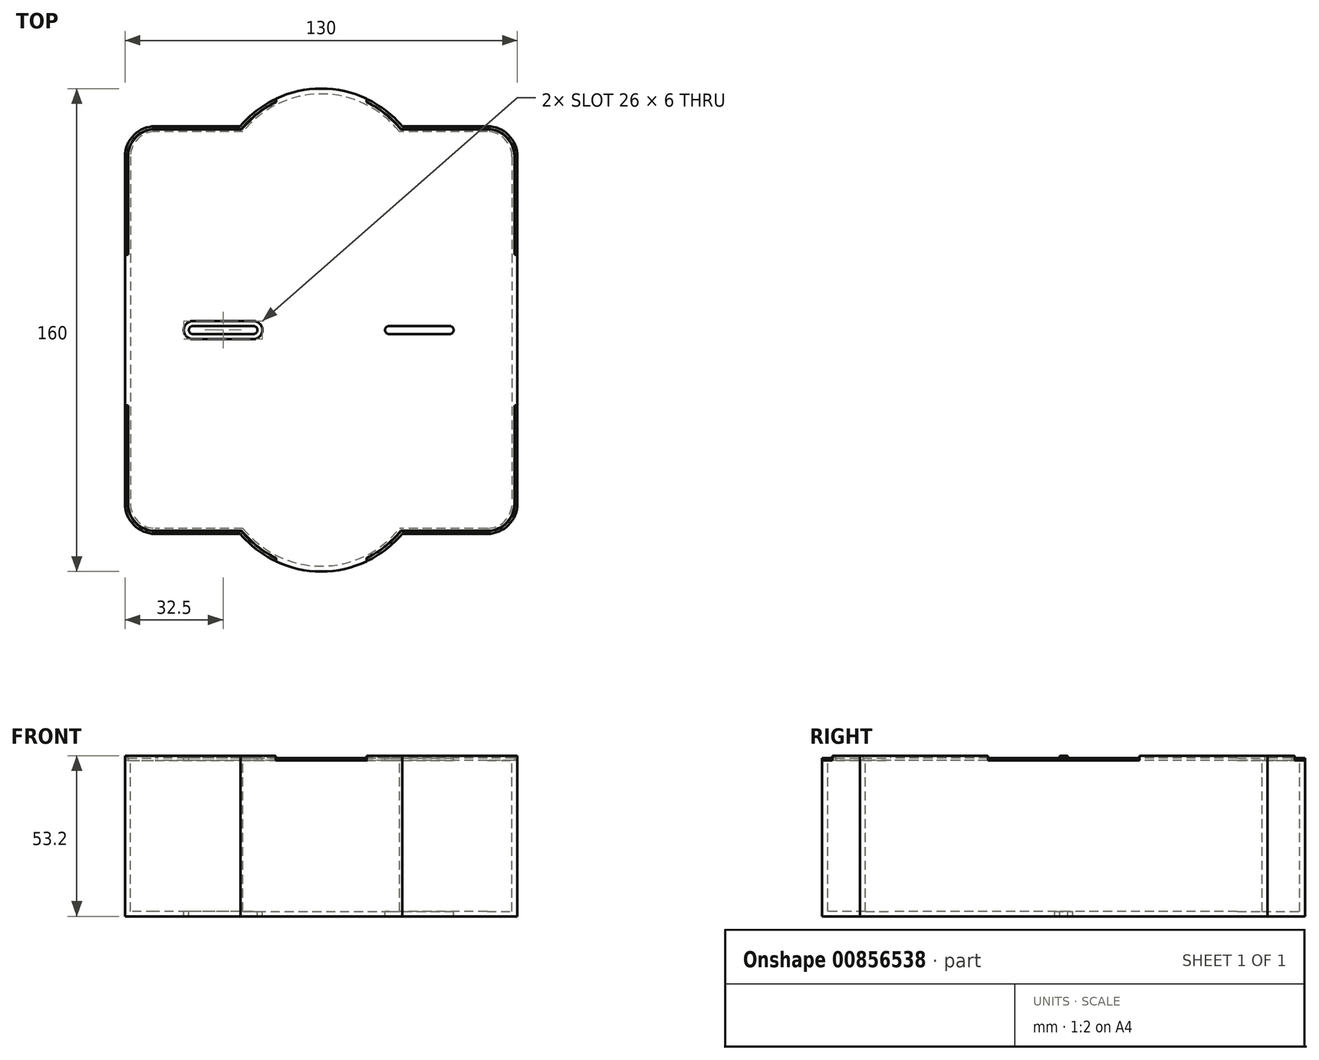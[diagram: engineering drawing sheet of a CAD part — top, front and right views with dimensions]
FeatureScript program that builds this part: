
annotation { "Feature Type Name" : "Feature", "Feature Type Description" : "" }
export const myFeature = defineFeature(function(context is Context, id is Id, definition is map)
    precondition{}
    {
        {
            var Q0;
            Q0=qCreatedBy(makeId("Top.planeOp"),FACE);
            var sketch = newSketch(context, id + "F0", { "sketchPlane" : qUnion([Q0])});
            skLineSegment(sketch, "E0.bottom", {"start": v(65, 67.5) * mm, "end": v(-65, 67.5) * mm, "construction": true});
            skLineSegment(sketch, "E0.top", {"start": v(65, -67.5) * mm, "end": v(-65, -67.5) * mm, "construction": true});
            skLineSegment(sketch, "E0.left", {"start": v(65, 67.5) * mm, "end": v(65, -67.5) * mm, "construction": true});
            skLineSegment(sketch, "E0.right", {"start": v(-65, 67.5) * mm, "end": v(-65, -67.5) * mm, "construction": true});
            skPoint(sketch, "E0.middle", {"position": v(0, 0) * mm});
            skArc(sketch, "E1", {"start": v(-26.8, 67.5) * mm, "mid": v(0, 80) * mm, "end": v(26.8, 67.5) * mm, "construction": true});
            skArc(sketch, "E2", {"start": v(-26.8, -67.5) * mm, "mid": v(0, -80) * mm, "end": v(26.8, -67.5) * mm, "construction": true});
            skSolve(sketch);
        }
        {
            var Q0;
            Q0=qCreatedBy(makeId("Top.planeOp"),FACE);
            var sketch = newSketch(context, id + "F1", { "sketchPlane" : qUnion([Q0])});
            skLineSegment(sketch, "E3.0", {"start": v(-65, 57.5) * mm, "end": v(-65, -57.5) * mm});
            skLineSegment(sketch, "E4.0", {"start": v(55, 67.5) * mm, "end": v(26.8, 67.5) * mm});
            skArc(sketch, "E5.0", {"start": v(-26.8, 67.5) * mm, "mid": v(0, 80) * mm, "end": v(26.8, 67.5) * mm});
            skLineSegment(sketch, "E6.0", {"start": v(65, 57.5) * mm, "end": v(65, -57.5) * mm});
            skLineSegment(sketch, "E7.0", {"start": v(55, -67.5) * mm, "end": v(26.8, -67.5) * mm});
            skArc(sketch, "E8.0", {"start": v(-26.8, -67.5) * mm, "mid": v(0, -80) * mm, "end": v(26.8, -67.5) * mm});
            skLineSegment(sketch, "E9.trimOffspring", {"start": v(-26.8, 67.5) * mm, "end": v(-55, 67.5) * mm});
            skLineSegment(sketch, "E10.trimOffspring", {"start": v(-26.8, -67.5) * mm, "end": v(-55, -67.5) * mm});
            skPoint(sketch, "E11.visualSharp", {"position": v(-65, 67.5) * mm});
            skArc(sketch, "E11.filletArc", {"start": v(-55, 67.5) * mm, "mid": v(-62.07, 64.57) * mm, "end": v(-65, 57.5) * mm});
            skPoint(sketch, "E12.visualSharp", {"position": v(65, 67.5) * mm});
            skArc(sketch, "E12.filletArc", {"start": v(65, 57.5) * mm, "mid": v(62.07, 64.57) * mm, "end": v(55, 67.5) * mm});
            skPoint(sketch, "E13.visualSharp", {"position": v(65, -67.5) * mm});
            skArc(sketch, "E13.filletArc", {"start": v(55, -67.5) * mm, "mid": v(62.07, -64.57) * mm, "end": v(65, -57.5) * mm});
            skPoint(sketch, "E14.visualSharp", {"position": v(-65, -67.5) * mm});
            skArc(sketch, "E14.filletArc", {"start": v(-65, -57.5) * mm, "mid": v(-62.07, -64.57) * mm, "end": v(-55, -67.5) * mm});
            skSolve(sketch);
        }
        {
            var Q0;
            Q0=qCreatedBy(makeId("Top.planeOp"),FACE);
            var sketch = newSketch(context, id + "F2", { "sketchPlane" : qUnion([Q0])});
            skArc(sketch, "E15.0", {"start": v(-55, 65.7) * mm, "mid": v(-60.8, 63.3) * mm, "end": v(-63.2, 57.5) * mm});
            skLineSegment(sketch, "E15.1", {"start": v(55, -65.7) * mm, "end": v(25.96, -65.7) * mm});
            skArc(sketch, "E15.2", {"start": v(-25.96, -65.7) * mm, "mid": v(0, -78.2) * mm, "end": v(25.96, -65.7) * mm});
            skLineSegment(sketch, "E15.3", {"start": v(-25.96, -65.7) * mm, "end": v(-55, -65.7) * mm});
            skArc(sketch, "E15.4", {"start": v(-63.2, -57.5) * mm, "mid": v(-60.8, -63.3) * mm, "end": v(-55, -65.7) * mm});
            skArc(sketch, "E15.5", {"start": v(55, -65.7) * mm, "mid": v(60.8, -63.3) * mm, "end": v(63.2, -57.5) * mm});
            skLineSegment(sketch, "E15.6", {"start": v(-63.2, 57.5) * mm, "end": v(-63.2, -57.5) * mm});
            skLineSegment(sketch, "E15.7", {"start": v(63.2, 57.5) * mm, "end": v(63.2, -57.5) * mm});
            skArc(sketch, "E15.8", {"start": v(63.2, 57.5) * mm, "mid": v(60.8, 63.3) * mm, "end": v(55, 65.7) * mm});
            skLineSegment(sketch, "E15.9", {"start": v(55, 65.7) * mm, "end": v(25.96, 65.7) * mm});
            skArc(sketch, "E15.10", {"start": v(-25.96, 65.7) * mm, "mid": v(0, 78.2) * mm, "end": v(25.96, 65.7) * mm});
            skLineSegment(sketch, "E15.11", {"start": v(-25.96, 65.7) * mm, "end": v(-55, 65.7) * mm});
            skLineSegment(sketch, "E16.0", {"start": v(-26.8, 67.5) * mm, "end": v(-55, 67.5) * mm});
            skArc(sketch, "E17.0", {"start": v(-26.8, 67.5) * mm, "mid": v(0, 80) * mm, "end": v(26.8, 67.5) * mm});
            skLineSegment(sketch, "E18.0", {"start": v(55, 67.5) * mm, "end": v(26.8, 67.5) * mm});
            skArc(sketch, "E19.0", {"start": v(65, 57.5) * mm, "mid": v(62.07, 64.57) * mm, "end": v(55, 67.5) * mm});
            skArc(sketch, "E20.0", {"start": v(-55, 67.5) * mm, "mid": v(-62.07, 64.57) * mm, "end": v(-65, 57.5) * mm});
            skLineSegment(sketch, "E20.1", {"start": v(-65, 57.5) * mm, "end": v(-65, -57.5) * mm});
            skLineSegment(sketch, "E20.2", {"start": v(65, 57.5) * mm, "end": v(65, -57.5) * mm});
            skArc(sketch, "E20.3", {"start": v(-65, -57.5) * mm, "mid": v(-62.07, -64.57) * mm, "end": v(-55, -67.5) * mm});
            skLineSegment(sketch, "E20.4", {"start": v(-26.8, -67.5) * mm, "end": v(-55, -67.5) * mm});
            skArc(sketch, "E20.5", {"start": v(-26.8, -67.5) * mm, "mid": v(0, -80) * mm, "end": v(26.8, -67.5) * mm});
            skLineSegment(sketch, "E20.6", {"start": v(55, -67.5) * mm, "end": v(26.8, -67.5) * mm});
            skArc(sketch, "E20.7", {"start": v(55, -67.5) * mm, "mid": v(62.07, -64.57) * mm, "end": v(65, -57.5) * mm});
            skSolve(sketch);
        }
        {
            var Q0;
            Q0=qCreatedBy(makeId("Front.planeOp"),FACE);
            var sketch = newSketch(context, id + "F3", { "sketchPlane" : qUnion([Q0])});
            skLineSegment(sketch, "E21", {"start": v(0, 0) * mm, "end": v(0, 50) * mm});
            skLineSegment(sketch, "E22", {"start": v(0, 0) * mm, "end": v(0, -1.6) * mm});
            skLineSegment(sketch, "E23", {"start": v(0, 50) * mm, "end": v(0, 51.6) * mm});
            skSolve(sketch);
        }
        {
            var Q0;
            Q0 = qSketchRegion(id + "F1", true);
            var Q1;
            Q1=sQuery(id+"F3.wireOp",EDGE,"E22");
            sweep(context, id + "F4", {"profiles" : qUnion([Q0]), "path" : qUnion([Q1])});
        }
        {
            var Q0;
            Q0 = qSketchRegion(id + "F2", true);
            var Q1;
            Q1=sQuery(id+"F3.wireOp",EDGE,"E21");
            var Q2;
            Q2=sQuery(id+"F3.wireOp",EDGE,"E23");
            sweep(context, id + "F5", {"operationType" : NewBodyOperationType.ADD, "profiles" : qUnion([Q0]), "path" : qUnion([Q1, Q2])});
        }
        {
            var Q0;
            Q0=makeQuery(id+"F5.opSweep","CAP_FACE",FACE,{"disambiguationData":[OSD([sQuery(id+"F2.wireOp",EDGE,"E15.0"),sQuery(id+"F2.wireOp",EDGE,"E15.1"),sQuery(id+"F2.wireOp",EDGE,"E15.2"),sQuery(id+"F2.wireOp",EDGE,"E15.3"),sQuery(id+"F2.wireOp",EDGE,"E15.4"),sQuery(id+"F2.wireOp",EDGE,"E15.5"),sQuery(id+"F2.wireOp",EDGE,"E15.6"),sQuery(id+"F2.wireOp",EDGE,"E15.7"),sQuery(id+"F2.wireOp",EDGE,"E15.8"),sQuery(id+"F2.wireOp",EDGE,"E15.9"),sQuery(id+"F2.wireOp",EDGE,"E15.10"),sQuery(id+"F2.wireOp",EDGE,"E15.11"),sQuery(id+"F2.wireOp",EDGE,"E16.0"),sQuery(id+"F2.wireOp",EDGE,"E17.0"),sQuery(id+"F2.wireOp",EDGE,"E18.0"),sQuery(id+"F2.wireOp",EDGE,"E19.0"),sQuery(id+"F2.wireOp",EDGE,"E20.0"),sQuery(id+"F2.wireOp",EDGE,"E20.1"),sQuery(id+"F2.wireOp",EDGE,"E20.2"),sQuery(id+"F2.wireOp",EDGE,"E20.3"),sQuery(id+"F2.wireOp",EDGE,"E20.4"),sQuery(id+"F2.wireOp",EDGE,"E20.5"),sQuery(id+"F2.wireOp",EDGE,"E20.6"),sQuery(id+"F2.wireOp",EDGE,"E20.7"),sQuery(id+"F3.wireOp",VERTEX,"E23.end")])],"isStart":false});
            var sketch = newSketch(context, id + "F6", { "sketchPlane" : qUnion([Q0])});
            skArc(sketch, "E24.0", {"start": v(-26.34, 66.5) * mm, "mid": v(-21.16, 71.62) * mm, "end": v(-15, 75.51) * mm});
            skLineSegment(sketch, "E24.1", {"start": v(-26.34, -66.5) * mm, "end": v(-55, -66.5) * mm});
            skArc(sketch, "E24.2", {"start": v(-64, -57.5) * mm, "mid": v(-61.36, -63.86) * mm, "end": v(-55, -66.5) * mm});
            skLineSegment(sketch, "E24.3", {"start": v(-64, 57.5) * mm, "end": v(-64, 25) * mm});
            skArc(sketch, "E24.4", {"start": v(-55, 66.5) * mm, "mid": v(-61.36, 63.86) * mm, "end": v(-64, 57.5) * mm});
            skArc(sketch, "E24.5", {"start": v(-26.34, -66.5) * mm, "mid": v(-21.16, -71.62) * mm, "end": v(-15, -75.51) * mm});
            skLineSegment(sketch, "E24.6", {"start": v(-26.34, 66.5) * mm, "end": v(-55, 66.5) * mm});
            skLineSegment(sketch, "E24.7", {"start": v(55, -66.5) * mm, "end": v(26.34, -66.5) * mm});
            skArc(sketch, "E24.8", {"start": v(55, -66.5) * mm, "mid": v(61.36, -63.86) * mm, "end": v(64, -57.5) * mm});
            skLineSegment(sketch, "E24.9", {"start": v(64, 57.5) * mm, "end": v(64, 25) * mm});
            skArc(sketch, "E24.10", {"start": v(64, 57.5) * mm, "mid": v(61.36, 63.86) * mm, "end": v(55, 66.5) * mm});
            skLineSegment(sketch, "E24.11", {"start": v(55, 66.5) * mm, "end": v(26.34, 66.5) * mm});
            skLineSegment(sketch, "E25.0", {"start": v(-65, 57.5) * mm, "end": v(-65, -57.5) * mm, "construction": true});
            skLineSegment(sketch, "E26.0", {"start": v(65, -57.5) * mm, "end": v(65, 57.5) * mm, "construction": true});
            skLineSegment(sketch, "E27.bottom", {"start": v(65, 25) * mm, "end": v(64, 25) * mm});
            skLineSegment(sketch, "E27.top", {"start": v(65, -25) * mm, "end": v(64, -25) * mm});
            skLineSegment(sketch, "E27.left", {"start": v(65, 25) * mm, "end": v(65, -25) * mm});
            skLineSegment(sketch, "E27.right", {"start": v(-65, 25) * mm, "end": v(-65, -25) * mm});
            skPoint(sketch, "E27.middle", {"position": v(0, 0) * mm});
            skLineSegment(sketch, "E28.trimOffspring", {"start": v(-64, 25) * mm, "end": v(-65, 25) * mm});
            skLineSegment(sketch, "E29.trimOffspring", {"start": v(-64, -25) * mm, "end": v(-65, -25) * mm});
            skLineSegment(sketch, "E30.trimOffspring", {"start": v(-64, -25) * mm, "end": v(-64, -57.5) * mm});
            skLineSegment(sketch, "E31.trimOffspring", {"start": v(64, -25) * mm, "end": v(64, -57.5) * mm});
            skArc(sketch, "E32.0", {"start": v(15, 76.62) * mm, "mid": v(0, 80) * mm, "end": v(-15, 76.62) * mm});
            skArc(sketch, "E33.0", {"start": v(-15, -76.62) * mm, "mid": v(0, -80) * mm, "end": v(15, -76.62) * mm});
            skLineSegment(sketch, "E34.left", {"start": v(15, 76.62) * mm, "end": v(15, 75.51) * mm});
            skLineSegment(sketch, "E34.right", {"start": v(-15, 76.62) * mm, "end": v(-15, 75.51) * mm});
            skPoint(sketch, "E34.top.end.orphan", {"position": v(-15, -97.47) * mm});
            skPoint(sketch, "E34.top.start.orphan", {"position": v(15, -97.47) * mm});
            skPoint(sketch, "E35.orphan", {"position": v(-15, 97.47) * mm});
            skPoint(sketch, "E36.orphan", {"position": v(15, 97.47) * mm});
            skLineSegment(sketch, "E37.trimOffspring", {"start": v(-15, -75.51) * mm, "end": v(-15, -76.62) * mm});
            skLineSegment(sketch, "E38.trimOffspring", {"start": v(15, -75.51) * mm, "end": v(15, -76.62) * mm});
            skPoint(sketch, "E39.orphan", {"position": v(-26.8, 67.5) * mm});
            skPoint(sketch, "E40.orphan", {"position": v(26.8, 67.5) * mm});
            skPoint(sketch, "E41.orphan", {"position": v(-26.8, -67.5) * mm});
            skPoint(sketch, "E42.orphan", {"position": v(26.8, -67.5) * mm});
            skArc(sketch, "E43.trimOffspring", {"start": v(15, -75.51) * mm, "mid": v(21.16, -71.62) * mm, "end": v(26.34, -66.5) * mm});
            skArc(sketch, "E44.trimOffspring", {"start": v(15, 75.51) * mm, "mid": v(21.16, 71.62) * mm, "end": v(26.34, 66.5) * mm});
            skSolve(sketch);
        }
        {
            var Q0;
            Q0=makeQuery(id+"F5.opSweep","CAP_FACE",FACE,{"disambiguationData":[OSD([sQuery(id+"F2.wireOp",EDGE,"E15.0"),sQuery(id+"F2.wireOp",EDGE,"E15.1"),sQuery(id+"F2.wireOp",EDGE,"E15.2"),sQuery(id+"F2.wireOp",EDGE,"E15.3"),sQuery(id+"F2.wireOp",EDGE,"E15.4"),sQuery(id+"F2.wireOp",EDGE,"E15.5"),sQuery(id+"F2.wireOp",EDGE,"E15.6"),sQuery(id+"F2.wireOp",EDGE,"E15.7"),sQuery(id+"F2.wireOp",EDGE,"E15.8"),sQuery(id+"F2.wireOp",EDGE,"E15.9"),sQuery(id+"F2.wireOp",EDGE,"E15.10"),sQuery(id+"F2.wireOp",EDGE,"E15.11"),sQuery(id+"F2.wireOp",EDGE,"E16.0"),sQuery(id+"F2.wireOp",EDGE,"E17.0"),sQuery(id+"F2.wireOp",EDGE,"E18.0"),sQuery(id+"F2.wireOp",EDGE,"E19.0"),sQuery(id+"F2.wireOp",EDGE,"E20.0"),sQuery(id+"F2.wireOp",EDGE,"E20.1"),sQuery(id+"F2.wireOp",EDGE,"E20.2"),sQuery(id+"F2.wireOp",EDGE,"E20.3"),sQuery(id+"F2.wireOp",EDGE,"E20.4"),sQuery(id+"F2.wireOp",EDGE,"E20.5"),sQuery(id+"F2.wireOp",EDGE,"E20.6"),sQuery(id+"F2.wireOp",EDGE,"E20.7"),sQuery(id+"F3.wireOp",VERTEX,"E23.end")])],"isStart":false});
            var sketch = newSketch(context, id + "F7", { "sketchPlane" : qUnion([Q0])});
            skArc(sketch, "E45.0", {"start": v(-26.39, 66.6) * mm, "mid": v(-21.22, 71.7) * mm, "end": v(-15.1, 75.57) * mm});
            skLineSegment(sketch, "E45.1", {"start": v(-15.1, 76.69) * mm, "end": v(-15.1, 75.57) * mm});
            skArc(sketch, "E45.2", {"start": v(15.1, 76.69) * mm, "mid": v(0, 80.1) * mm, "end": v(-15.1, 76.69) * mm});
            skLineSegment(sketch, "E45.3", {"start": v(15.1, 76.69) * mm, "end": v(15.1, 75.57) * mm});
            skArc(sketch, "E45.4", {"start": v(15.1, 75.57) * mm, "mid": v(21.22, 71.7) * mm, "end": v(26.39, 66.6) * mm});
            skLineSegment(sketch, "E45.5", {"start": v(-15.1, -75.57) * mm, "end": v(-15.1, -76.69) * mm});
            skArc(sketch, "E45.6", {"start": v(-26.39, -66.6) * mm, "mid": v(-21.22, -71.7) * mm, "end": v(-15.1, -75.57) * mm});
            skLineSegment(sketch, "E45.7", {"start": v(-26.39, -66.6) * mm, "end": v(-55, -66.6) * mm});
            skArc(sketch, "E45.8", {"start": v(-64.1, -57.5) * mm, "mid": v(-61.43, -63.93) * mm, "end": v(-55, -66.6) * mm});
            skLineSegment(sketch, "E45.9", {"start": v(-64.1, -25.1) * mm, "end": v(-64.1, -57.5) * mm});
            skLineSegment(sketch, "E45.10", {"start": v(-64.1, -25.1) * mm, "end": v(-65.1, -25.1) * mm});
            skArc(sketch, "E45.11", {"start": v(-55, 66.6) * mm, "mid": v(-61.43, 63.93) * mm, "end": v(-64.1, 57.5) * mm});
            skLineSegment(sketch, "E45.12", {"start": v(-64.1, 57.5) * mm, "end": v(-64.1, 25.1) * mm});
            skLineSegment(sketch, "E45.13", {"start": v(-64.1, 25.1) * mm, "end": v(-65.1, 25.1) * mm});
            skLineSegment(sketch, "E45.14", {"start": v(-65.1, 25.1) * mm, "end": v(-65.1, -25.1) * mm});
            skArc(sketch, "E45.15", {"start": v(-15.1, -76.69) * mm, "mid": v(0, -80.1) * mm, "end": v(15.1, -76.69) * mm});
            skLineSegment(sketch, "E45.16", {"start": v(15.1, -75.57) * mm, "end": v(15.1, -76.69) * mm});
            skArc(sketch, "E45.17", {"start": v(15.1, -75.57) * mm, "mid": v(21.22, -71.7) * mm, "end": v(26.39, -66.6) * mm});
            skLineSegment(sketch, "E45.18", {"start": v(55, -66.6) * mm, "end": v(26.39, -66.6) * mm});
            skArc(sketch, "E45.19", {"start": v(55, -66.6) * mm, "mid": v(61.43, -63.93) * mm, "end": v(64.1, -57.5) * mm});
            skLineSegment(sketch, "E45.20", {"start": v(-26.39, 66.6) * mm, "end": v(-55, 66.6) * mm});
            skLineSegment(sketch, "E45.21", {"start": v(64.1, -25.1) * mm, "end": v(64.1, -57.5) * mm});
            skLineSegment(sketch, "E45.22", {"start": v(65.1, -25.1) * mm, "end": v(64.1, -25.1) * mm});
            skLineSegment(sketch, "E45.23", {"start": v(65.1, 25.1) * mm, "end": v(65.1, -25.1) * mm});
            skLineSegment(sketch, "E45.24", {"start": v(65.1, 25.1) * mm, "end": v(64.1, 25.1) * mm});
            skLineSegment(sketch, "E45.25", {"start": v(64.1, 57.5) * mm, "end": v(64.1, 25.1) * mm});
            skArc(sketch, "E45.26", {"start": v(64.1, 57.5) * mm, "mid": v(61.43, 63.93) * mm, "end": v(55, 66.6) * mm});
            skLineSegment(sketch, "E45.27", {"start": v(55, 66.6) * mm, "end": v(26.39, 66.6) * mm});
            skSolve(sketch);
        }
        {
            var Q0;
            Q0 = qSketchRegion(id + "F7", true);
            var Q1;
            Q1=sQuery(id+"F3.wireOp",EDGE,"E23");
            sweep(context, id + "F8", {"operationType" : NewBodyOperationType.REMOVE, "profiles" : qUnion([Q0]), "path" : qUnion([Q1])});
        }
        {
            var Q0;
            Q0 = qSketchRegion(id + "F6", true);
            var Q1;
            Q1=sQuery(id+"F3.wireOp",EDGE,"E23");
            sweep(context, id + "F9", {"profiles" : qUnion([Q0]), "path" : qUnion([Q1])});
        }
        {
            var Q0;
            Q0=makeQuery(id+"F9.opSweep","CAP_FACE",FACE,{"disambiguationData":[OSD([sQuery(id+"F3.wireOp",VERTEX,"E23.end"),sQuery(id+"F6.wireOp",EDGE,"E24.0"),sQuery(id+"F6.wireOp",EDGE,"E24.1"),sQuery(id+"F6.wireOp",EDGE,"E24.2"),sQuery(id+"F6.wireOp",EDGE,"E24.3"),sQuery(id+"F6.wireOp",EDGE,"E24.4"),sQuery(id+"F6.wireOp",EDGE,"E24.5"),sQuery(id+"F6.wireOp",EDGE,"E24.6"),sQuery(id+"F6.wireOp",EDGE,"E24.7"),sQuery(id+"F6.wireOp",EDGE,"E24.8"),sQuery(id+"F6.wireOp",EDGE,"E24.9"),sQuery(id+"F6.wireOp",EDGE,"E24.10"),sQuery(id+"F6.wireOp",EDGE,"E24.11"),sQuery(id+"F6.wireOp",EDGE,"E27.bottom"),sQuery(id+"F6.wireOp",EDGE,"E27.top"),sQuery(id+"F6.wireOp",EDGE,"E27.left"),sQuery(id+"F6.wireOp",EDGE,"E27.right"),sQuery(id+"F6.wireOp",EDGE,"E28.trimOffspring"),sQuery(id+"F6.wireOp",EDGE,"E29.trimOffspring"),sQuery(id+"F6.wireOp",EDGE,"E30.trimOffspring"),sQuery(id+"F6.wireOp",EDGE,"E31.trimOffspring"),sQuery(id+"F6.wireOp",EDGE,"E32.0"),sQuery(id+"F6.wireOp",EDGE,"E33.0"),sQuery(id+"F6.wireOp",EDGE,"E34.left"),sQuery(id+"F6.wireOp",EDGE,"E34.right"),sQuery(id+"F6.wireOp",EDGE,"E37.trimOffspring"),sQuery(id+"F6.wireOp",EDGE,"E38.trimOffspring"),sQuery(id+"F6.wireOp",EDGE,"E43.trimOffspring"),sQuery(id+"F6.wireOp",EDGE,"E44.trimOffspring")])],"isStart":true});
            var sketch = newSketch(context, id + "F10", { "sketchPlane" : qUnion([Q0])});
            skLineSegment(sketch, "E46", {"start": v(-22.5, 0) * mm, "end": v(-42.5, 0) * mm, "construction": true});
            skLineSegment(sketch, "E47", {"start": v(0, 0) * mm, "end": v(0, 25.22) * mm, "construction": true});
            skArc(sketch, "E48.0.startCap", {"start": v(-22.5, 3) * mm, "mid": v(-19.5, 0) * mm, "end": v(-22.5, -3) * mm});
            skArc(sketch, "E48.0.endCap", {"start": v(-42.5, -3) * mm, "mid": v(-45.5, 0) * mm, "end": v(-42.5, 3) * mm});
            skLineSegment(sketch, "E48.0.left", {"start": v(-22.5, -3) * mm, "end": v(-42.5, -3) * mm});
            skLineSegment(sketch, "E48.0.right", {"start": v(-22.5, 3) * mm, "end": v(-42.5, 3) * mm});
            skArc(sketch, "E49.0.startCap", {"start": v(-22.5, 1.35) * mm, "mid": v(-21.15, 0) * mm, "end": v(-22.5, -1.35) * mm});
            skArc(sketch, "E49.0.endCap", {"start": v(-42.5, -1.35) * mm, "mid": v(-43.85, 0) * mm, "end": v(-42.5, 1.35) * mm});
            skLineSegment(sketch, "E49.0.left", {"start": v(-22.5, -1.35) * mm, "end": v(-42.5, -1.35) * mm});
            skLineSegment(sketch, "E49.0.right", {"start": v(-22.5, 1.35) * mm, "end": v(-42.5, 1.35) * mm});
            skArc(sketch, "E50.MirrorCS", {"start": v(22.5, 3) * mm, "mid": v(19.5, 0) * mm, "end": v(22.5, -3) * mm});
            skArc(sketch, "E51.MirrorCS", {"start": v(22.5, 1.35) * mm, "mid": v(21.15, 0) * mm, "end": v(22.5, -1.35) * mm});
            skLineSegment(sketch, "E52.MirrorCS", {"start": v(22.5, 3) * mm, "end": v(42.5, 3) * mm});
            skLineSegment(sketch, "E53.MirrorCS", {"start": v(22.5, 1.35) * mm, "end": v(42.5, 1.35) * mm});
            skLineSegment(sketch, "E54.MirrorCS", {"start": v(22.5, -1.35) * mm, "end": v(42.5, -1.35) * mm});
            skLineSegment(sketch, "E55.MirrorCS", {"start": v(22.5, -3) * mm, "end": v(42.5, -3) * mm});
            skArc(sketch, "E56.MirrorCS", {"start": v(42.5, -1.35) * mm, "mid": v(43.85, 0) * mm, "end": v(42.5, 1.35) * mm});
            skArc(sketch, "E57.MirrorCS", {"start": v(42.5, -3) * mm, "mid": v(45.5, 0) * mm, "end": v(42.5, 3) * mm});
            skSolve(sketch);
        }
        {
            var Q0;
            Q0=makeQuery(id+"F10.imprint","IMPRINT",FACE,{"disambiguationData":[TD([[makeQuery(id+"F10.imprint","IMPRINT",EDGE,{"derivedFrom":sQuery(id+"F10.wireOp",EDGE,"E49.0.startCap")}),-1.0]])]});
            var Q1;
            Q1=makeQuery(id+"F10.imprint","IMPRINT",FACE,{"disambiguationData":[TD([[makeQuery(id+"F10.imprint","IMPRINT",EDGE,{"derivedFrom":sQuery(id+"F10.wireOp",EDGE,"E51.MirrorCS")}),1.0]])]});
            extrude(context, id + "F11", {"entities" : qUnion([Q0, Q1]), "operationType" : NewBodyOperationType.REMOVE, "endBound" : BoundingType.THROUGH_ALL, "oppositeDirection" : true, "depth" : 25 * mm, "offsetDistance" : 25 * mm});
        }
        {
            var Q0;
            Q0=makeQuery(id+"F10.imprint","IMPRINT",FACE,{"disambiguationData":[TD([[makeQuery(id+"F10.imprint","IMPRINT",EDGE,{"derivedFrom":sQuery(id+"F10.wireOp",EDGE,"E48.0.startCap")}),-1.0]])]});
            var Q1;
            Q1=makeQuery(id+"F10.imprint","IMPRINT",FACE,{"disambiguationData":[TD([[makeQuery(id+"F10.imprint","IMPRINT",EDGE,{"derivedFrom":sQuery(id+"F10.wireOp",EDGE,"E50.MirrorCS")}),1.0]])]});
            extrude(context, id + "F12", {"entities" : qUnion([Q0, Q1]), "operationType" : NewBodyOperationType.REMOVE, "oppositeDirection" : true, "depth" : 0.8 * mm, "offsetDistance" : 25 * mm});
        }
    });
